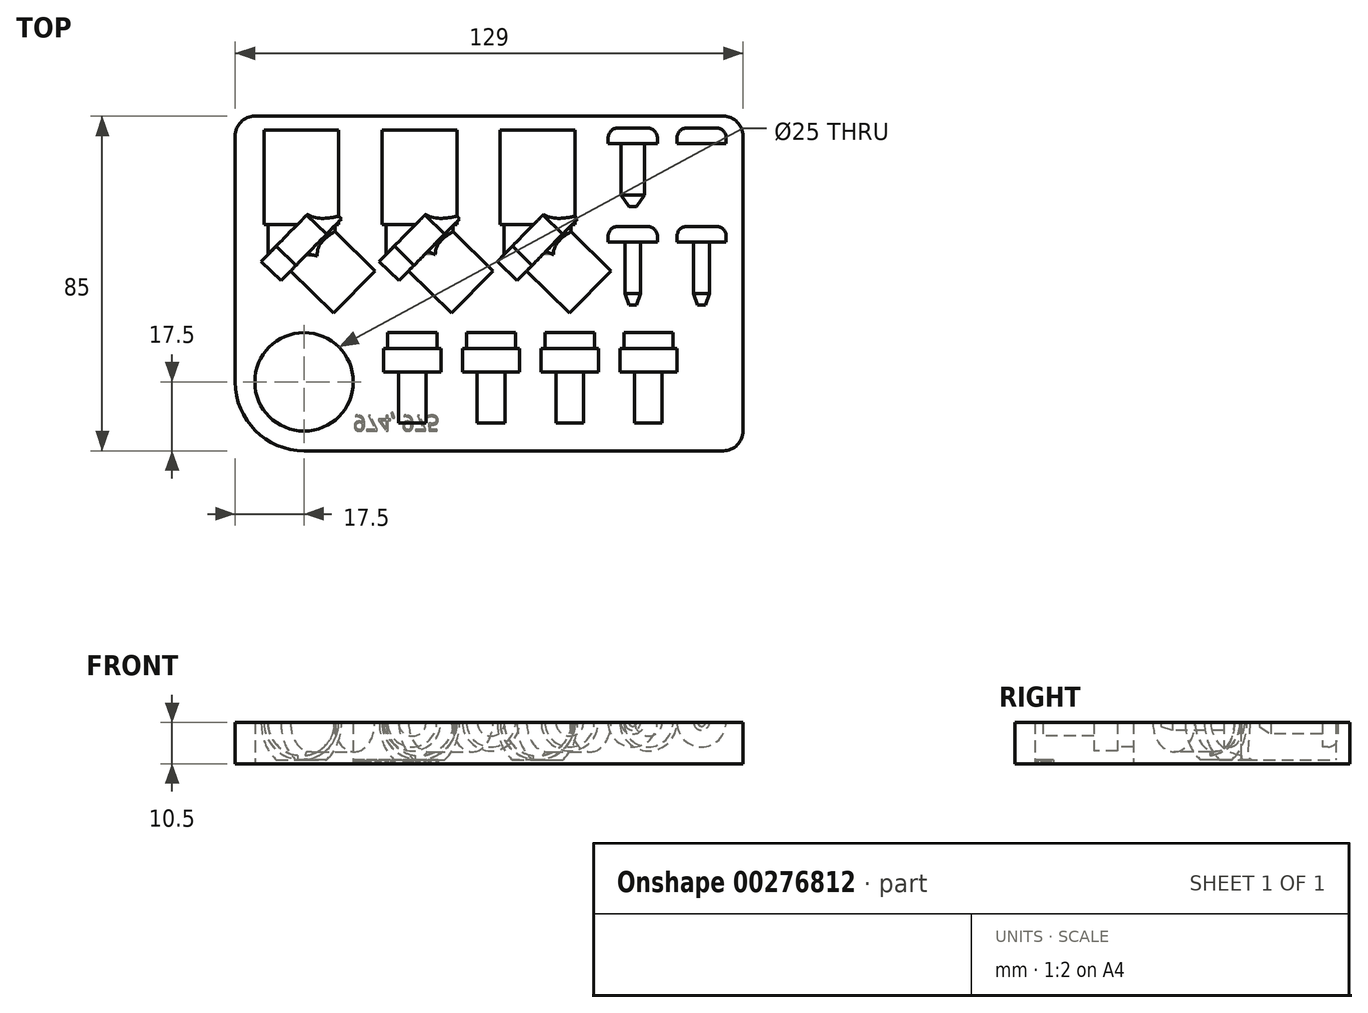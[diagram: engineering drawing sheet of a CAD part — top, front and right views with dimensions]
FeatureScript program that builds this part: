
annotation { "Feature Type Name" : "Feature", "Feature Type Description" : "" }
export const myFeature = defineFeature(function(context is Context, id is Id, definition is map)
    precondition{}
    {
        {
            var Q0;
            Q0=qCreatedBy(makeId("Top.planeOp"),FACE);
            var sketch = newSketch(context, id + "F0", { "sketchPlane" : qUnion([Q0])});
            skLineSegment(sketch, "E0.bottom", {"start": v(17.5, 0) * mm, "end": v(124, 0) * mm});
            skLineSegment(sketch, "E0.top", {"start": v(5, 85) * mm, "end": v(124, 85) * mm});
            skLineSegment(sketch, "E0.left", {"start": v(0, 17.5) * mm, "end": v(0, 80) * mm});
            skLineSegment(sketch, "E0.right", {"start": v(129, 5) * mm, "end": v(129, 80) * mm});
            skLineSegment(sketch, "E1.bottom", {"start": v(17.5, 0) * mm, "end": v(17.5, 0) * mm});
            skLineSegment(sketch, "E1.top", {"start": v(0, 17.5) * mm, "end": v(17.5, 17.5) * mm, "construction": true});
            skLineSegment(sketch, "E1.left", {"start": v(0, 17.5) * mm, "end": v(0, 17.5) * mm});
            skLineSegment(sketch, "E1.right", {"start": v(17.5, 0) * mm, "end": v(17.5, 17.5) * mm, "construction": true});
            skCircle(sketch, "E2", {"center": v(17.5, 17.5) * mm, "radius": 12.5 * mm});
            skPoint(sketch, "E3.visualSharp", {"position": v(0, 0) * mm});
            skArc(sketch, "E3.filletArc", {"start": v(0, 17.5) * mm, "mid": v(5.13, 5.13) * mm, "end": v(17.5, 0) * mm});
            skPoint(sketch, "E4.visualSharp", {"position": v(0, 85) * mm});
            skArc(sketch, "E4.filletArc", {"start": v(5, 85) * mm, "mid": v(1.46, 83.54) * mm, "end": v(0, 80) * mm});
            skPoint(sketch, "E5.visualSharp", {"position": v(129, 85) * mm});
            skArc(sketch, "E5.filletArc", {"start": v(129, 80) * mm, "mid": v(127.54, 83.54) * mm, "end": v(124, 85) * mm});
            skPoint(sketch, "E6.visualSharp", {"position": v(129, 0) * mm});
            skArc(sketch, "E6.filletArc", {"start": v(124, 0) * mm, "mid": v(127.54, 1.46) * mm, "end": v(129, 5) * mm});
            skSolve(sketch);
        }
        {
            var Q0;
            Q0=makeQuery(id+"F0.imprint","IMPRINT",FACE,{"disambiguationData":[TD([[makeQuery(id+"F0.imprint","IMPRINT",EDGE,{"derivedFrom":sQuery(id+"F0.wireOp",EDGE,"E0.bottom")}),1.0]])]});
            extrude(context, id + "F1", {"entities" : qUnion([Q0]), "depth" : 10.5 * mm});
        }
        {
            var Q0;
            Q0=makeQuery(id+"F1.opExtrude","CAP_FACE",FACE,{"disambiguationData":[OSD([sQuery(id+"F0.wireOp",EDGE,"E0.bottom"),sQuery(id+"F0.wireOp",EDGE,"E0.top"),sQuery(id+"F0.wireOp",EDGE,"E0.left"),sQuery(id+"F0.wireOp",EDGE,"E0.right"),sQuery(id+"F0.wireOp",EDGE,"E2"),sQuery(id+"F0.wireOp",EDGE,"E3.filletArc"),sQuery(id+"F0.wireOp",EDGE,"E4.filletArc"),sQuery(id+"F0.wireOp",EDGE,"E5.filletArc"),sQuery(id+"F0.wireOp",EDGE,"E6.filletArc")])],"isStart":false});
            var sketch = newSketch(context, id + "F2", { "sketchPlane" : qUnion([Q0])});
            skLineSegment(sketch, "E7.bottom", {"start": v(0, 0) * mm, "end": v(25, 0) * mm, "construction": true});
            skLineSegment(sketch, "E7.top", {"start": v(0, 35) * mm, "end": v(25, 35) * mm, "construction": true});
            skLineSegment(sketch, "E7.left", {"start": v(0, 0) * mm, "end": v(0, 35) * mm, "construction": true});
            skLineSegment(sketch, "E7.right", {"start": v(25, 0) * mm, "end": v(25, 35) * mm, "construction": true});
            skLineSegment(sketch, "E8", {"start": v(25, 35) * mm, "end": v(14.07, 45.7) * mm});
            skLineSegment(sketch, "E9", {"start": v(14.07, 45.7) * mm, "end": v(11.62, 43.2) * mm});
            skLineSegment(sketch, "E10", {"start": v(11.62, 43.2) * mm, "end": v(6.62, 48.1) * mm});
            skLineSegment(sketch, "E11", {"start": v(6.62, 48.1) * mm, "end": v(14.32, 55.96) * mm});
            skLineSegment(sketch, "E12", {"start": v(14.32, 55.96) * mm, "end": v(30.25, 40.36) * mm});
            skLineSegment(sketch, "E13", {"start": v(25, 35) * mm, "end": v(30.25, 40.36) * mm});
            skLineSegment(sketch, "E14", {"start": v(14.32, 55.96) * mm, "end": v(16.82, 53.51) * mm, "construction": true});
            skLineSegment(sketch, "E15", {"start": v(16.82, 53.51) * mm, "end": v(16.82, 81.51) * mm});
            skLineSegment(sketch, "E16", {"start": v(16.82, 81.51) * mm, "end": v(7.32, 81.51) * mm});
            skLineSegment(sketch, "E17", {"start": v(7.32, 81.51) * mm, "end": v(7.32, 57.51) * mm});
            skLineSegment(sketch, "E18", {"start": v(7.32, 57.51) * mm, "end": v(8.32, 57.51) * mm});
            skLineSegment(sketch, "E19", {"start": v(8.32, 57.51) * mm, "end": v(8.32, 53.16) * mm});
            skLineSegment(sketch, "E20", {"start": v(46.82, 53.51) * mm, "end": v(46.82, 81.51) * mm});
            skLineSegment(sketch, "E21", {"start": v(46.82, 81.51) * mm, "end": v(37.32, 81.51) * mm});
            skLineSegment(sketch, "E22", {"start": v(37.32, 81.51) * mm, "end": v(37.32, 57.51) * mm});
            skLineSegment(sketch, "E23", {"start": v(37.32, 57.51) * mm, "end": v(38.32, 57.51) * mm});
            skLineSegment(sketch, "E24", {"start": v(76.82, 53.51) * mm, "end": v(76.82, 81.51) * mm});
            skLineSegment(sketch, "E25", {"start": v(76.82, 81.51) * mm, "end": v(67.32, 81.51) * mm});
            skLineSegment(sketch, "E26", {"start": v(67.32, 81.51) * mm, "end": v(67.32, 57.51) * mm});
            skLineSegment(sketch, "E27", {"start": v(67.32, 57.51) * mm, "end": v(68.32, 57.51) * mm});
            skLineSegment(sketch, "E28", {"start": v(8.32, 57.51) * mm, "end": v(8.32, 49.51) * mm});
            skLineSegment(sketch, "E29", {"start": v(8.32, 49.51) * mm, "end": v(16.82, 53.51) * mm});
            skLineSegment(sketch, "E30", {"start": v(38.32, 57.51) * mm, "end": v(38.32, 49.51) * mm});
            skLineSegment(sketch, "E31", {"start": v(38.32, 49.51) * mm, "end": v(46.82, 53.51) * mm});
            skLineSegment(sketch, "E32", {"start": v(68.32, 57.51) * mm, "end": v(68.32, 49.51) * mm});
            skLineSegment(sketch, "E33", {"start": v(68.32, 49.51) * mm, "end": v(76.82, 53.51) * mm});
            skLineSegment(sketch, "E34", {"start": v(46.82, 53.51) * mm, "end": v(44.32, 55.96) * mm});
            skLineSegment(sketch, "E35", {"start": v(44.32, 55.96) * mm, "end": v(36.62, 48.1) * mm});
            skLineSegment(sketch, "E36", {"start": v(36.62, 48.1) * mm, "end": v(41.62, 43.2) * mm});
            skLineSegment(sketch, "E37", {"start": v(41.62, 43.2) * mm, "end": v(44.07, 45.7) * mm});
            skLineSegment(sketch, "E38", {"start": v(44.07, 45.7) * mm, "end": v(55, 35) * mm});
            skLineSegment(sketch, "E39", {"start": v(55, 35) * mm, "end": v(60.25, 40.36) * mm});
            skLineSegment(sketch, "E40", {"start": v(46.82, 53.51) * mm, "end": v(60.25, 40.36) * mm});
            skLineSegment(sketch, "E41", {"start": v(76.82, 53.51) * mm, "end": v(74.32, 55.96) * mm});
            skLineSegment(sketch, "E42", {"start": v(74.32, 55.96) * mm, "end": v(66.62, 48.1) * mm});
            skLineSegment(sketch, "E43", {"start": v(66.62, 48.1) * mm, "end": v(71.62, 43.2) * mm});
            skLineSegment(sketch, "E44", {"start": v(71.62, 43.2) * mm, "end": v(74.07, 45.7) * mm});
            skLineSegment(sketch, "E45", {"start": v(74.07, 45.7) * mm, "end": v(85, 35) * mm});
            skLineSegment(sketch, "E46", {"start": v(76.82, 53.51) * mm, "end": v(90.25, 40.36) * mm});
            skLineSegment(sketch, "E47", {"start": v(85, 35) * mm, "end": v(90.25, 40.36) * mm});
            skLineSegment(sketch, "E48", {"start": v(16.82, 53.51) * mm, "end": v(46.82, 53.51) * mm, "construction": true});
            skLineSegment(sketch, "E49", {"start": v(46.82, 53.51) * mm, "end": v(76.82, 53.51) * mm, "construction": true});
            skSolve(sketch);
        }
        {
            var Q0;
            {var subQ0=sQuery(id+"F2.wireOp",EDGE,"E15");Q0=makeQuery(id+"F2.imprint","IMPRINT",FACE,{"disambiguationData":[TD([[makeQuery(id+"F2.imprint","IMPRINT",EDGE,{"derivedFrom":subQ0}),1.0]])]});}
            var Q1;
            {var subQ5=sQuery(id+"F2.wireOp",EDGE,"E29");Q1=makeQuery(id+"F2.imprint","IMPRINT",FACE,{"disambiguationData":[TD([[makeQuery(id+"F2.imprint","IMPRINT",EDGE,{"derivedFrom":subQ5}),1.0]])]});}
            var Q2;
            Q2=sQuery(id+"F2.wireOp",EDGE,"E15");
            revolve(context, id + "F3", {"operationType" : NewBodyOperationType.REMOVE, "entities" : qUnion([Q0, Q1]), "axis" : qUnion([Q2]), "revolveType" : RevolveType.FULL, "oppositeDirection" : true});
        }
        {
            var Q0;
            Q0=makeQuery(id+"F2.imprint","IMPRINT",FACE,{"disambiguationData":[TD([[makeQuery(id+"F2.imprint","IMPRINT",EDGE,{"derivedFrom":sQuery(id+"F2.wireOp",EDGE,"E20")}),1.0]])]});
            var Q1;
            Q1=sQuery(id+"F2.wireOp",EDGE,"E20");
            revolve(context, id + "F4", {"operationType" : NewBodyOperationType.REMOVE, "entities" : qUnion([Q0]), "axis" : qUnion([Q1]), "revolveType" : RevolveType.FULL, "oppositeDirection" : true});
        }
        {
            var Q0;
            Q0=makeQuery(id+"F2.imprint","IMPRINT",FACE,{"disambiguationData":[TD([[makeQuery(id+"F2.imprint","IMPRINT",EDGE,{"derivedFrom":sQuery(id+"F2.wireOp",EDGE,"E24")}),1.0]])]});
            var Q1;
            Q1=sQuery(id+"F2.wireOp",EDGE,"E24");
            revolve(context, id + "F5", {"operationType" : NewBodyOperationType.REMOVE, "entities" : qUnion([Q0]), "axis" : qUnion([Q1]), "revolveType" : RevolveType.FULL, "oppositeDirection" : true});
        }
        {
            var Q0;
            Q0=makeQuery(id+"F2.imprint","IMPRINT",FACE,{"disambiguationData":[TD([[makeQuery(id+"F2.imprint","IMPRINT",EDGE,{"derivedFrom":sQuery(id+"F2.wireOp",EDGE,"E8")}),-1.0]])]});
            var Q1;
            {var subQ5=sQuery(id+"F2.wireOp",EDGE,"E29");Q1=makeQuery(id+"F2.imprint","IMPRINT",FACE,{"disambiguationData":[TD([[makeQuery(id+"F2.imprint","IMPRINT",EDGE,{"derivedFrom":subQ5}),1.0]])]});}
            var Q2;
            Q2=sQuery(id+"F2.wireOp",EDGE,"E12");
            revolve(context, id + "F6", {"operationType" : NewBodyOperationType.REMOVE, "entities" : qUnion([Q0, Q1]), "axis" : qUnion([Q2]), "revolveType" : RevolveType.FULL, "oppositeDirection" : true});
        }
        {
            var Q0;
            {var subQ4=sQuery(id+"F2.wireOp",EDGE,"E31");Q0=makeQuery(id+"F2.imprint","IMPRINT",FACE,{"disambiguationData":[TD([[makeQuery(id+"F2.imprint","IMPRINT",EDGE,{"derivedFrom":subQ4}),-1.0]])]});}
            var Q1;
            {var subQ0=sQuery(id+"F2.wireOp",EDGE,"E31");Q1=makeQuery(id+"F2.imprint","IMPRINT",FACE,{"disambiguationData":[TD([[makeQuery(id+"F2.imprint","IMPRINT",EDGE,{"derivedFrom":subQ0}),1.0]])]});}
            var Q2;
            Q2=sQuery(id+"F2.wireOp",EDGE,"E40");
            revolve(context, id + "F7", {"operationType" : NewBodyOperationType.REMOVE, "entities" : qUnion([Q0, Q1]), "axis" : qUnion([Q2]), "revolveType" : RevolveType.FULL, "oppositeDirection" : true});
        }
        {
            var Q0;
            {var subQ4=sQuery(id+"F2.wireOp",EDGE,"E33");Q0=makeQuery(id+"F2.imprint","IMPRINT",FACE,{"disambiguationData":[TD([[makeQuery(id+"F2.imprint","IMPRINT",EDGE,{"derivedFrom":subQ4}),-1.0]])]});}
            var Q1;
            {var subQ0=sQuery(id+"F2.wireOp",EDGE,"E33");Q1=makeQuery(id+"F2.imprint","IMPRINT",FACE,{"disambiguationData":[TD([[makeQuery(id+"F2.imprint","IMPRINT",EDGE,{"derivedFrom":subQ0}),1.0]])]});}
            var Q2;
            Q2=sQuery(id+"F2.wireOp",EDGE,"E46");
            revolve(context, id + "F8", {"operationType" : NewBodyOperationType.REMOVE, "entities" : qUnion([Q0, Q1]), "axis" : qUnion([Q2]), "revolveType" : RevolveType.FULL, "oppositeDirection" : true});
        }
        {
            var Q0;
            Q0=makeQuery(id+"F1.opExtrude","CAP_FACE",FACE,{"disambiguationData":[OSD([sQuery(id+"F0.wireOp",EDGE,"E0.bottom"),sQuery(id+"F0.wireOp",EDGE,"E0.top"),sQuery(id+"F0.wireOp",EDGE,"E0.left"),sQuery(id+"F0.wireOp",EDGE,"E0.right"),sQuery(id+"F0.wireOp",EDGE,"E2"),sQuery(id+"F0.wireOp",EDGE,"E3.filletArc"),sQuery(id+"F0.wireOp",EDGE,"E4.filletArc"),sQuery(id+"F0.wireOp",EDGE,"E5.filletArc"),sQuery(id+"F0.wireOp",EDGE,"E6.filletArc")])],"isStart":false});
            var sketch = newSketch(context, id + "F9", { "sketchPlane" : qUnion([Q0])});
            skLineSegment(sketch, "E50.0.0", {"start": v(124, 85) * mm, "end": v(5, 85) * mm});
            skArc(sketch, "E50.0.1", {"start": v(5, 85) * mm, "mid": v(1.46, 83.54) * mm, "end": v(0, 80) * mm});
            skLineSegment(sketch, "E50.0.2", {"start": v(0, 80) * mm, "end": v(0, 17.5) * mm});
            skArc(sketch, "E50.0.3", {"start": v(0, 17.5) * mm, "mid": v(5.13, 5.13) * mm, "end": v(17.5, 0) * mm});
            skLineSegment(sketch, "E50.0.4", {"start": v(17.5, 0) * mm, "end": v(124, 0) * mm});
            skArc(sketch, "E50.0.5", {"start": v(124, 0) * mm, "mid": v(127.54, 1.46) * mm, "end": v(129, 5) * mm});
            skLineSegment(sketch, "E50.0.6", {"start": v(129, 5) * mm, "end": v(129, 80) * mm});
            skArc(sketch, "E50.0.7", {"start": v(129, 80) * mm, "mid": v(127.54, 83.54) * mm, "end": v(124, 85) * mm});
            skCircle(sketch, "E51.0", {"center": v(17.5, 17.5) * mm, "radius": 12.5 * mm});
            skSolve(sketch);
        }
        {
            var Q0;
            Q0=qSketchRegion(id+"F9",true);
            extrude(context, id + "F10", {"entities" : qUnion([Q0]), "operationType" : NewBodyOperationType.ADD, "oppositeDirection" : true, "depth" : 10.5 * mm, "hasSecondDirection" : true, "secondDirectionOppositeDirection" : true, "secondDirectionDepth" : 9.5 * mm});
        }
        {
            var Q0;
            Q0=makeQuery(id+"F1.opExtrude","CAP_FACE",FACE,{"disambiguationData":[OSD([sQuery(id+"F0.wireOp",EDGE,"E0.bottom"),sQuery(id+"F0.wireOp",EDGE,"E0.top"),sQuery(id+"F0.wireOp",EDGE,"E0.left"),sQuery(id+"F0.wireOp",EDGE,"E0.right"),sQuery(id+"F0.wireOp",EDGE,"E2"),sQuery(id+"F0.wireOp",EDGE,"E3.filletArc"),sQuery(id+"F0.wireOp",EDGE,"E4.filletArc"),sQuery(id+"F0.wireOp",EDGE,"E5.filletArc"),sQuery(id+"F0.wireOp",EDGE,"E6.filletArc")])],"isStart":false});
            var sketch = newSketch(context, id + "F11", { "sketchPlane" : qUnion([Q0])});
            skLineSegment(sketch, "E52.bottom", {"start": v(0, 0) * mm, "end": v(101, 0) * mm, "construction": true});
            skLineSegment(sketch, "E52.top", {"start": v(0, 82) * mm, "end": v(101, 82) * mm, "construction": true});
            skLineSegment(sketch, "E52.left", {"start": v(0, 0) * mm, "end": v(0, 82) * mm, "construction": true});
            skLineSegment(sketch, "E52.right", {"start": v(101, 0) * mm, "end": v(101, 82) * mm, "construction": true});
            skLineSegment(sketch, "E53.bottom", {"start": v(101, 82) * mm, "end": v(104.75, 82) * mm});
            skLineSegment(sketch, "E53.top", {"start": v(104, 78) * mm, "end": v(107.25, 78) * mm});
            skLineSegment(sketch, "E53.left", {"start": v(101, 82) * mm, "end": v(101, 78) * mm});
            skLineSegment(sketch, "E53.right", {"start": v(107.25, 79.5) * mm, "end": v(107.25, 78) * mm});
            skPoint(sketch, "E54.visualSharp", {"position": v(107.25, 82) * mm});
            skArc(sketch, "E54.filletArc", {"start": v(107.25, 79.5) * mm, "mid": v(106.52, 81.27) * mm, "end": v(104.75, 82) * mm});
            skLineSegment(sketch, "E55.left", {"start": v(101, 78) * mm, "end": v(101, 72) * mm});
            skLineSegment(sketch, "E55.right", {"start": v(104, 78) * mm, "end": v(104, 65) * mm});
            skLineSegment(sketch, "E56", {"start": v(101, 82) * mm, "end": v(118.5, 82) * mm, "construction": true});
            skLineSegment(sketch, "E57.bottom", {"start": v(118.5, 82) * mm, "end": v(122.25, 82) * mm});
            skLineSegment(sketch, "E57.top", {"start": v(118.5, 78) * mm, "end": v(124.75, 78) * mm});
            skLineSegment(sketch, "E57.left", {"start": v(118.5, 82) * mm, "end": v(118.5, 78) * mm});
            skLineSegment(sketch, "E57.right", {"start": v(124.75, 79.5) * mm, "end": v(124.75, 78) * mm});
            skLineSegment(sketch, "E58.bottom", {"start": v(118.5, 78) * mm, "end": v(121.5, 78) * mm});
            skLineSegment(sketch, "E58.top", {"start": v(118.5, 62) * mm, "end": v(119.5, 62) * mm});
            skLineSegment(sketch, "E58.left", {"start": v(118.5, 78) * mm, "end": v(118.5, 62) * mm});
            skLineSegment(sketch, "E58.right", {"start": v(121.5, 78) * mm, "end": v(121.5, 65) * mm});
            skPoint(sketch, "E59.visualSharp", {"position": v(124.75, 82) * mm});
            skArc(sketch, "E59.filletArc", {"start": v(124.75, 79.5) * mm, "mid": v(124.02, 81.27) * mm, "end": v(122.25, 82) * mm});
            skLineSegment(sketch, "E60", {"start": v(118.5, 62) * mm, "end": v(119.5, 62) * mm, "construction": true});
            skLineSegment(sketch, "E61", {"start": v(119.5, 62) * mm, "end": v(121.5, 65) * mm});
            skLineSegment(sketch, "E62", {"start": v(101, 78) * mm, "end": v(101, 62) * mm});
            skLineSegment(sketch, "E63", {"start": v(101, 62) * mm, "end": v(102, 62) * mm});
            skLineSegment(sketch, "E64", {"start": v(102, 62) * mm, "end": v(104, 65) * mm});
            skLineSegment(sketch, "E65", {"start": v(101, 62) * mm, "end": v(101, 57) * mm, "construction": true});
            skLineSegment(sketch, "E66.bottom", {"start": v(101, 57) * mm, "end": v(104.75, 57) * mm});
            skLineSegment(sketch, "E66.top", {"start": v(103, 53) * mm, "end": v(107.25, 53) * mm});
            skLineSegment(sketch, "E66.left", {"start": v(101, 57) * mm, "end": v(101, 53) * mm});
            skLineSegment(sketch, "E66.right", {"start": v(107.25, 54.5) * mm, "end": v(107.25, 53) * mm});
            skLineSegment(sketch, "E67.left", {"start": v(101, 53) * mm, "end": v(101, 37) * mm});
            skLineSegment(sketch, "E68", {"start": v(103, 53) * mm, "end": v(103, 40) * mm});
            skLineSegment(sketch, "E69", {"start": v(101, 37) * mm, "end": v(102, 37) * mm});
            skLineSegment(sketch, "E70", {"start": v(102, 37) * mm, "end": v(103, 40) * mm});
            skPoint(sketch, "E71.visualSharp", {"position": v(107.25, 57) * mm});
            skArc(sketch, "E71.filletArc", {"start": v(107.25, 54.5) * mm, "mid": v(106.52, 56.27) * mm, "end": v(104.75, 57) * mm});
            skLineSegment(sketch, "E72", {"start": v(101, 57) * mm, "end": v(118.5, 57) * mm, "construction": true});
            skLineSegment(sketch, "E73.bottom", {"start": v(118.5, 57) * mm, "end": v(122.25, 57) * mm});
            skLineSegment(sketch, "E73.top", {"start": v(120.5, 53) * mm, "end": v(124.75, 53) * mm});
            skLineSegment(sketch, "E73.left", {"start": v(118.5, 57) * mm, "end": v(118.5, 53) * mm});
            skLineSegment(sketch, "E73.right", {"start": v(124.75, 54.5) * mm, "end": v(124.75, 53) * mm});
            skLineSegment(sketch, "E74.left", {"start": v(118.5, 53) * mm, "end": v(118.5, 37) * mm});
            skLineSegment(sketch, "E75", {"start": v(120.5, 53) * mm, "end": v(120.5, 40) * mm});
            skLineSegment(sketch, "E76", {"start": v(118.5, 37) * mm, "end": v(119.5, 37) * mm});
            skLineSegment(sketch, "E77", {"start": v(119.5, 37) * mm, "end": v(120.5, 40) * mm});
            skPoint(sketch, "E78.visualSharp", {"position": v(124.75, 57) * mm});
            skArc(sketch, "E78.filletArc", {"start": v(124.75, 54.5) * mm, "mid": v(124.02, 56.27) * mm, "end": v(122.25, 57) * mm});
            skSolve(sketch);
        }
        {
            var Q0;
            Q0=makeQuery(id+"F11.imprint","IMPRINT",FACE,{"disambiguationData":[TD([[makeQuery(id+"F11.imprint","IMPRINT",EDGE,{"derivedFrom":sQuery(id+"F11.wireOp",EDGE,"E53.bottom")}),-1.0]])]});
            var Q1;
            Q1=makeQuery(id+"F11.imprint","IMPRINT",FACE,{"disambiguationData":[TD([[makeQuery(id+"F11.imprint","IMPRINT",EDGE,{"derivedFrom":sQuery(id+"F11.wireOp",EDGE,"E66.bottom")}),-1.0]])]});
            var Q2;
            Q2=sQuery(id+"F11.wireOp",EDGE,"E67.left");
            revolve(context, id + "F12", {"operationType" : NewBodyOperationType.REMOVE, "entities" : qUnion([Q0, Q1]), "axis" : qUnion([Q2]), "revolveType" : RevolveType.FULL, "oppositeDirection" : true});
        }
        {
            var Q0;
            Q0=makeQuery(id+"F11.imprint","IMPRINT",FACE,{"disambiguationData":[TD([[makeQuery(id+"F11.imprint","IMPRINT",EDGE,{"derivedFrom":sQuery(id+"F11.wireOp",EDGE,"E58.bottom")}),-1.0]])]});
            var Q1;
            Q1=makeQuery(id+"F11.imprint","IMPRINT",FACE,{"disambiguationData":[TD([[makeQuery(id+"F11.imprint","IMPRINT",EDGE,{"derivedFrom":sQuery(id+"F11.wireOp",EDGE,"E57.bottom")}),-1.0]])]});
            var Q2;
            Q2=makeQuery(id+"F11.imprint","IMPRINT",FACE,{"disambiguationData":[TD([[makeQuery(id+"F11.imprint","IMPRINT",EDGE,{"derivedFrom":sQuery(id+"F11.wireOp",EDGE,"E73.bottom")}),-1.0]])]});
            var Q3;
            Q3=sQuery(id+"F11.wireOp",EDGE,"E74.left");
            revolve(context, id + "F13", {"operationType" : NewBodyOperationType.REMOVE, "entities" : qUnion([Q0, Q1, Q2]), "axis" : qUnion([Q3]), "revolveType" : RevolveType.FULL, "oppositeDirection" : true});
        }
        {
            var Q0;
            Q0=makeQuery(id+"F1.opExtrude","CAP_FACE",FACE,{"disambiguationData":[OSD([sQuery(id+"F0.wireOp",EDGE,"E0.bottom"),sQuery(id+"F0.wireOp",EDGE,"E0.top"),sQuery(id+"F0.wireOp",EDGE,"E0.left"),sQuery(id+"F0.wireOp",EDGE,"E0.right"),sQuery(id+"F0.wireOp",EDGE,"E2"),sQuery(id+"F0.wireOp",EDGE,"E3.filletArc"),sQuery(id+"F0.wireOp",EDGE,"E4.filletArc"),sQuery(id+"F0.wireOp",EDGE,"E5.filletArc"),sQuery(id+"F0.wireOp",EDGE,"E6.filletArc")])],"isStart":false});
            var sketch = newSketch(context, id + "F14", { "sketchPlane" : qUnion([Q0])});
            skLineSegment(sketch, "E79.bottom", {"start": v(0, 0) * mm, "end": v(45, 0) * mm, "construction": true});
            skLineSegment(sketch, "E79.top", {"start": v(0, 30) * mm, "end": v(45, 30) * mm, "construction": true});
            skLineSegment(sketch, "E79.left", {"start": v(0, 0) * mm, "end": v(0, 30) * mm, "construction": true});
            skLineSegment(sketch, "E79.right", {"start": v(45, 0) * mm, "end": v(45, 17.5) * mm, "construction": true});
            skLineSegment(sketch, "E80.bottom", {"start": v(45, 30) * mm, "end": v(51.25, 30) * mm});
            skLineSegment(sketch, "E80.left", {"start": v(45, 30) * mm, "end": v(45, 26) * mm});
            skLineSegment(sketch, "E80.right", {"start": v(51.25, 30) * mm, "end": v(51.25, 26) * mm});
            skLineSegment(sketch, "E81.bottom", {"start": v(51.25, 26) * mm, "end": v(52.25, 26) * mm});
            skLineSegment(sketch, "E81.left", {"start": v(45, 26) * mm, "end": v(45, 17.5) * mm});
            skPoint(sketch, "E81.right.end.orphan", {"position": v(47.25, 17.5) * mm});
            skLineSegment(sketch, "E82.trimOffspring", {"start": v(45, 26) * mm, "end": v(45, 30) * mm, "construction": true});
            skLineSegment(sketch, "E83", {"start": v(52.25, 26) * mm, "end": v(52.25, 20) * mm});
            skLineSegment(sketch, "E84", {"start": v(52.25, 20) * mm, "end": v(48.5, 20) * mm});
            skLineSegment(sketch, "E85", {"start": v(45, 20) * mm, "end": v(45, 26) * mm});
            skLineSegment(sketch, "E86.top", {"start": v(45, 7) * mm, "end": v(48.5, 7) * mm});
            skLineSegment(sketch, "E86.left", {"start": v(45, 20) * mm, "end": v(45, 7) * mm});
            skLineSegment(sketch, "E86.right", {"start": v(48.5, 20) * mm, "end": v(48.5, 7) * mm});
            skLineSegment(sketch, "E87", {"start": v(45, 30) * mm, "end": v(65, 30) * mm, "construction": true});
            skLineSegment(sketch, "E88", {"start": v(65, 30) * mm, "end": v(85, 30) * mm, "construction": true});
            skLineSegment(sketch, "E89", {"start": v(85, 30) * mm, "end": v(105, 30) * mm, "construction": true});
            skLineSegment(sketch, "E90.bottom", {"start": v(65, 30) * mm, "end": v(71.25, 30) * mm});
            skLineSegment(sketch, "E90.left", {"start": v(65, 30) * mm, "end": v(65, 26) * mm});
            skLineSegment(sketch, "E90.right", {"start": v(71.25, 30) * mm, "end": v(71.25, 26) * mm});
            skLineSegment(sketch, "E91.bottom", {"start": v(85, 30) * mm, "end": v(91.25, 30) * mm});
            skLineSegment(sketch, "E91.left", {"start": v(85, 30) * mm, "end": v(85, 26) * mm});
            skLineSegment(sketch, "E91.right", {"start": v(91.25, 30) * mm, "end": v(91.25, 26) * mm});
            skLineSegment(sketch, "E92.bottom", {"start": v(105, 30) * mm, "end": v(111.25, 30) * mm});
            skLineSegment(sketch, "E92.left", {"start": v(105, 30) * mm, "end": v(105, 26) * mm});
            skLineSegment(sketch, "E92.right", {"start": v(111.25, 30) * mm, "end": v(111.25, 26) * mm});
            skLineSegment(sketch, "E93.bottom", {"start": v(71.25, 26) * mm, "end": v(72.25, 26) * mm});
            skLineSegment(sketch, "E93.top", {"start": v(68.5, 20) * mm, "end": v(72.25, 20) * mm});
            skLineSegment(sketch, "E93.left", {"start": v(65, 26) * mm, "end": v(65, 20) * mm});
            skLineSegment(sketch, "E93.right", {"start": v(72.25, 26) * mm, "end": v(72.25, 20) * mm});
            skLineSegment(sketch, "E94.bottom", {"start": v(91.25, 26) * mm, "end": v(92.25, 26) * mm});
            skLineSegment(sketch, "E94.top", {"start": v(88.5, 20) * mm, "end": v(92.25, 20) * mm});
            skLineSegment(sketch, "E94.left", {"start": v(85, 26) * mm, "end": v(85, 20) * mm});
            skLineSegment(sketch, "E94.right", {"start": v(92.25, 26) * mm, "end": v(92.25, 20) * mm});
            skLineSegment(sketch, "E95.bottom", {"start": v(111.25, 26) * mm, "end": v(112.25, 26) * mm});
            skLineSegment(sketch, "E95.top", {"start": v(108.5, 20) * mm, "end": v(112.25, 20) * mm});
            skLineSegment(sketch, "E95.left", {"start": v(105, 26) * mm, "end": v(105, 20) * mm});
            skLineSegment(sketch, "E95.right", {"start": v(112.25, 26) * mm, "end": v(112.25, 20) * mm});
            skLineSegment(sketch, "E96.top", {"start": v(65, 7) * mm, "end": v(68.5, 7) * mm});
            skLineSegment(sketch, "E96.left", {"start": v(65, 20) * mm, "end": v(65, 7) * mm});
            skLineSegment(sketch, "E96.right", {"start": v(68.5, 20) * mm, "end": v(68.5, 7) * mm});
            skLineSegment(sketch, "E97.top", {"start": v(85, 7) * mm, "end": v(88.5, 7) * mm});
            skLineSegment(sketch, "E97.left", {"start": v(85, 20) * mm, "end": v(85, 7) * mm});
            skLineSegment(sketch, "E97.right", {"start": v(88.5, 20) * mm, "end": v(88.5, 7) * mm});
            skLineSegment(sketch, "E98.top", {"start": v(105, 7) * mm, "end": v(108.5, 7) * mm});
            skLineSegment(sketch, "E98.left", {"start": v(105, 20) * mm, "end": v(105, 7) * mm});
            skLineSegment(sketch, "E98.right", {"start": v(108.5, 20) * mm, "end": v(108.5, 7) * mm});
            skSolve(sketch);
        }
        {
            var Q0;
            Q0=makeQuery(id+"F14.imprint","IMPRINT",FACE,{"disambiguationData":[TD([[makeQuery(id+"F14.imprint","IMPRINT",EDGE,{"derivedFrom":sQuery(id+"F14.wireOp",EDGE,"E80.bottom")}),-1.0]])]});
            var Q1;
            Q1=sQuery(id+"F14.wireOp",EDGE,"E86.left");
            revolve(context, id + "F15", {"operationType" : NewBodyOperationType.REMOVE, "entities" : qUnion([Q0]), "axis" : qUnion([Q1]), "revolveType" : RevolveType.FULL, "oppositeDirection" : true});
        }
        {
            var Q0;
            Q0=makeQuery(id+"F14.imprint","IMPRINT",FACE,{"disambiguationData":[TD([[makeQuery(id+"F14.imprint","IMPRINT",EDGE,{"derivedFrom":sQuery(id+"F14.wireOp",EDGE,"E90.bottom")}),-1.0]])]});
            var Q1;
            Q1=sQuery(id+"F14.wireOp",EDGE,"E96.left");
            revolve(context, id + "F16", {"operationType" : NewBodyOperationType.REMOVE, "entities" : qUnion([Q0]), "axis" : qUnion([Q1]), "revolveType" : RevolveType.FULL, "oppositeDirection" : true});
        }
        {
            var Q0;
            Q0=makeQuery(id+"F14.imprint","IMPRINT",FACE,{"disambiguationData":[TD([[makeQuery(id+"F14.imprint","IMPRINT",EDGE,{"derivedFrom":sQuery(id+"F14.wireOp",EDGE,"E91.bottom")}),-1.0]])]});
            var Q1;
            Q1=sQuery(id+"F14.wireOp",EDGE,"E97.left");
            revolve(context, id + "F17", {"operationType" : NewBodyOperationType.REMOVE, "entities" : qUnion([Q0]), "axis" : qUnion([Q1]), "revolveType" : RevolveType.FULL, "oppositeDirection" : true});
        }
        {
            var Q0;
            Q0=makeQuery(id+"F14.imprint","IMPRINT",FACE,{"disambiguationData":[TD([[makeQuery(id+"F14.imprint","IMPRINT",EDGE,{"derivedFrom":sQuery(id+"F14.wireOp",EDGE,"E92.bottom")}),-1.0]])]});
            var Q1;
            Q1=sQuery(id+"F14.wireOp",EDGE,"E98.left");
            revolve(context, id + "F18", {"operationType" : NewBodyOperationType.REMOVE, "entities" : qUnion([Q0]), "axis" : qUnion([Q1]), "revolveType" : RevolveType.FULL, "oppositeDirection" : true});
        }
        {
            var Q0;
            Q0=makeQuery(id+"F10.boolean.opBoolean","MERGE",FACE,{"derivedFrom":[makeQuery(id+"F1.opExtrude","CAP_FACE",FACE,{"disambiguationData":[OSD([sQuery(id+"F0.wireOp",EDGE,"E0.bottom"),sQuery(id+"F0.wireOp",EDGE,"E0.top"),sQuery(id+"F0.wireOp",EDGE,"E0.left"),sQuery(id+"F0.wireOp",EDGE,"E0.right"),sQuery(id+"F0.wireOp",EDGE,"E2"),sQuery(id+"F0.wireOp",EDGE,"E3.filletArc"),sQuery(id+"F0.wireOp",EDGE,"E4.filletArc"),sQuery(id+"F0.wireOp",EDGE,"E5.filletArc"),sQuery(id+"F0.wireOp",EDGE,"E6.filletArc")])],"isStart":true}),makeQuery(id+"F10.opExtrude","CAP_FACE",FACE,{"disambiguationData":[OSD([sQuery(id+"F9.wireOp",EDGE,"E50.0.0"),sQuery(id+"F9.wireOp",EDGE,"E50.0.1"),sQuery(id+"F9.wireOp",EDGE,"E50.0.2"),sQuery(id+"F9.wireOp",EDGE,"E50.0.3"),sQuery(id+"F9.wireOp",EDGE,"E50.0.4"),sQuery(id+"F9.wireOp",EDGE,"E50.0.5"),sQuery(id+"F9.wireOp",EDGE,"E50.0.6"),sQuery(id+"F9.wireOp",EDGE,"E50.0.7"),sQuery(id+"F9.wireOp",EDGE,"E51.0")])],"isStart":false})]});
            var sketch = newSketch(context, id + "F19", { "sketchPlane" : qUnion([Q0])});
            skLineSegment(sketch, "E99.bottom", {"start": v(0, 0) * mm, "end": v(30, 0) * mm, "construction": true});
            skLineSegment(sketch, "E99.top", {"start": v(0, -5) * mm, "end": v(30, -5) * mm, "construction": true});
            skLineSegment(sketch, "E99.left", {"start": v(0, 0) * mm, "end": v(0, -5) * mm, "construction": true});
            skLineSegment(sketch, "E99.right", {"start": v(30, 0) * mm, "end": v(30, -5) * mm, "construction": true});
            skText(sketch, "E100", { "text": "974, 975", "fontName": "OpenSans-Regular.ttf"});
            const initialGuessF19  = {"E100": [0.03, -0.009, 1, 0, 0.004]};
            skSetInitialGuess(sketch, initialGuessF19);
            skSolve(sketch);
        }
        {
            var Q0;
            Q0 = qSketchRegion(id + "F19", true);
            extrude(context, id + "F20", {"entities" : qUnion([Q0]), "operationType" : NewBodyOperationType.REMOVE, "oppositeDirection" : true, "depth" : 1 * mm});
        }
        {
            var Q0;
            Q0=makeQuery(id+"F1.opExtrude","CAP_FACE",FACE,{"disambiguationData":[OSD([sQuery(id+"F0.wireOp",EDGE,"E0.bottom"),sQuery(id+"F0.wireOp",EDGE,"E0.top"),sQuery(id+"F0.wireOp",EDGE,"E0.left"),sQuery(id+"F0.wireOp",EDGE,"E0.right"),sQuery(id+"F0.wireOp",EDGE,"E2"),sQuery(id+"F0.wireOp",EDGE,"E3.filletArc"),sQuery(id+"F0.wireOp",EDGE,"E4.filletArc"),sQuery(id+"F0.wireOp",EDGE,"E5.filletArc"),sQuery(id+"F0.wireOp",EDGE,"E6.filletArc")])],"isStart":false});
            var sketch = newSketch(context, id + "F21", { "sketchPlane" : qUnion([Q0])});
            skLineSegment(sketch, "E101.0", {"start": v(0, 17.5) * mm, "end": v(0, 80) * mm});
            skArc(sketch, "E102.0", {"start": v(5, 85) * mm, "mid": v(1.46, 83.54) * mm, "end": v(0, 80) * mm});
            skLineSegment(sketch, "E103.0", {"start": v(5, 85) * mm, "end": v(124, 85) * mm});
            skArc(sketch, "E104.0", {"start": v(129, 80) * mm, "mid": v(127.54, 83.54) * mm, "end": v(124, 85) * mm});
            skLineSegment(sketch, "E105.0", {"start": v(129, 5) * mm, "end": v(129, 80) * mm});
            skArc(sketch, "E106.0", {"start": v(124, 0) * mm, "mid": v(127.54, 1.46) * mm, "end": v(129, 5) * mm});
            skLineSegment(sketch, "E107.0", {"start": v(17.5, 0) * mm, "end": v(124, 0) * mm});
            skLineSegment(sketch, "E108.0", {"start": v(98.75, 30) * mm, "end": v(111.25, 30) * mm});
            skLineSegment(sketch, "E109.0", {"start": v(98.75, 26) * mm, "end": v(98.75, 30) * mm});
            skLineSegment(sketch, "E110.0", {"start": v(97.75, 26) * mm, "end": v(98.75, 26) * mm});
            skLineSegment(sketch, "E111.0", {"start": v(97.75, 20) * mm, "end": v(97.75, 26) * mm});
            skLineSegment(sketch, "E112.0", {"start": v(97.75, 20) * mm, "end": v(101.5, 20) * mm});
            skLineSegment(sketch, "E113.0", {"start": v(101.5, 7) * mm, "end": v(101.5, 20) * mm});
            skLineSegment(sketch, "E114.0", {"start": v(108.5, 20) * mm, "end": v(108.5, 7) * mm});
            skLineSegment(sketch, "E115.0", {"start": v(112.25, 26) * mm, "end": v(112.25, 20) * mm});
            skPoint(sketch, "E116.0", {"position": v(111.75, 26) * mm});
            skLineSegment(sketch, "E117.0", {"start": v(111.25, 26) * mm, "end": v(112.25, 26) * mm});
            skLineSegment(sketch, "E118.0", {"start": v(111.25, 30) * mm, "end": v(111.25, 26) * mm});
            skLineSegment(sketch, "E119.0", {"start": v(108.5, 20) * mm, "end": v(112.25, 20) * mm});
            skLineSegment(sketch, "E120.0", {"start": v(101.5, 7) * mm, "end": v(108.5, 7) * mm});
            skLineSegment(sketch, "E121.0", {"start": v(81.5, 7) * mm, "end": v(88.5, 7) * mm});
            skLineSegment(sketch, "E122.0", {"start": v(81.5, 7) * mm, "end": v(81.5, 20) * mm});
            skLineSegment(sketch, "E123.0", {"start": v(88.5, 20) * mm, "end": v(88.5, 7) * mm});
            skLineSegment(sketch, "E124.0", {"start": v(88.5, 20) * mm, "end": v(92.25, 20) * mm});
            skLineSegment(sketch, "E125.0", {"start": v(92.25, 26) * mm, "end": v(92.25, 20) * mm});
            skLineSegment(sketch, "E126.0", {"start": v(91.25, 26) * mm, "end": v(92.25, 26) * mm});
            skLineSegment(sketch, "E127.0", {"start": v(91.25, 30) * mm, "end": v(91.25, 26) * mm});
            skPoint(sketch, "E128.0", {"position": v(78.25, 26) * mm});
            skLineSegment(sketch, "E129.0", {"start": v(77.75, 20) * mm, "end": v(77.75, 26) * mm});
            skLineSegment(sketch, "E130.0", {"start": v(77.75, 20) * mm, "end": v(81.5, 20) * mm});
            skLineSegment(sketch, "E131.0", {"start": v(77.75, 26) * mm, "end": v(78.75, 26) * mm});
            skLineSegment(sketch, "E132.0", {"start": v(78.75, 26) * mm, "end": v(78.75, 30) * mm});
            skLineSegment(sketch, "E133.0", {"start": v(78.75, 30) * mm, "end": v(91.25, 30) * mm});
            skLineSegment(sketch, "E134.0", {"start": v(58.75, 26) * mm, "end": v(58.75, 30) * mm});
            skLineSegment(sketch, "E135.0", {"start": v(58.75, 30) * mm, "end": v(71.25, 30) * mm});
            skLineSegment(sketch, "E136.0", {"start": v(71.25, 30) * mm, "end": v(71.25, 26) * mm});
            skLineSegment(sketch, "E137.0", {"start": v(71.25, 26) * mm, "end": v(72.25, 26) * mm});
            skLineSegment(sketch, "E138.0", {"start": v(72.25, 26) * mm, "end": v(72.25, 20) * mm});
            skLineSegment(sketch, "E139.0", {"start": v(68.5, 20) * mm, "end": v(72.25, 20) * mm});
            skLineSegment(sketch, "E140.0", {"start": v(68.5, 20) * mm, "end": v(68.5, 7) * mm});
            skLineSegment(sketch, "E141.0", {"start": v(61.5, 7) * mm, "end": v(68.5, 7) * mm});
            skLineSegment(sketch, "E142.0", {"start": v(61.5, 7) * mm, "end": v(61.5, 20) * mm});
            skLineSegment(sketch, "E143.0", {"start": v(57.75, 20) * mm, "end": v(61.5, 20) * mm});
            skLineSegment(sketch, "E144.0", {"start": v(57.75, 20) * mm, "end": v(57.75, 26) * mm});
            skLineSegment(sketch, "E145.0", {"start": v(52.25, 20) * mm, "end": v(48.5, 20) * mm});
            skLineSegment(sketch, "E146.0", {"start": v(48.5, 20) * mm, "end": v(48.5, 7) * mm});
            skLineSegment(sketch, "E147.0", {"start": v(52.25, 26) * mm, "end": v(52.25, 20) * mm});
            skLineSegment(sketch, "E148.0", {"start": v(41.5, 7) * mm, "end": v(48.5, 7) * mm});
            skLineSegment(sketch, "E149.0", {"start": v(41.5, 7) * mm, "end": v(41.5, 20) * mm});
            skLineSegment(sketch, "E150.0", {"start": v(41.5, 20) * mm, "end": v(37.75, 20) * mm});
            skLineSegment(sketch, "E151.0", {"start": v(37.75, 20) * mm, "end": v(37.75, 26) * mm});
            skLineSegment(sketch, "E152.0", {"start": v(37.75, 26) * mm, "end": v(38.75, 26) * mm});
            skLineSegment(sketch, "E153.0", {"start": v(38.75, 26) * mm, "end": v(38.75, 30) * mm});
            skLineSegment(sketch, "E154.0", {"start": v(38.75, 30) * mm, "end": v(51.25, 30) * mm});
            skPoint(sketch, "E155.0", {"position": v(51.25, 28) * mm});
            skLineSegment(sketch, "E156.0", {"start": v(51.25, 30) * mm, "end": v(51.25, 26) * mm});
            skLineSegment(sketch, "E157.0", {"start": v(51.25, 26) * mm, "end": v(52.25, 26) * mm});
            skCircle(sketch, "E158.0", {"center": v(17.5, 17.5) * mm, "radius": 12.5 * mm});
            skArc(sketch, "E159.0", {"start": v(0, 17.5) * mm, "mid": v(5.13, 5.13) * mm, "end": v(17.5, 0) * mm});
            skLineSegment(sketch, "E160.0", {"start": v(35.5, 45.72) * mm, "end": v(25.32, 55.69) * mm});
            skLineSegment(sketch, "E161.0", {"start": v(35.5, 45.72) * mm, "end": v(25, 35) * mm});
            skLineSegment(sketch, "E162.0", {"start": v(14.07, 45.7) * mm, "end": v(25, 35) * mm});
            skLineSegment(sketch, "E163.0", {"start": v(11.62, 43.2) * mm, "end": v(14.07, 45.7) * mm});
            skLineSegment(sketch, "E164.0", {"start": v(6.62, 48.1) * mm, "end": v(11.62, 43.2) * mm});
            skLineSegment(sketch, "E165.0", {"start": v(8.32, 49.84) * mm, "end": v(6.62, 48.1) * mm});
            skLineSegment(sketch, "E166.0", {"start": v(8.32, 57.51) * mm, "end": v(8.32, 49.84) * mm});
            skLineSegment(sketch, "E167.0", {"start": v(25.32, 55.69) * mm, "end": v(25.32, 57.19) * mm});
            skLineSegment(sketch, "E168.0", {"start": v(25.32, 57.19) * mm, "end": v(25.64, 57.51) * mm});
            skLineSegment(sketch, "E169.0", {"start": v(25.64, 57.51) * mm, "end": v(26.32, 57.51) * mm});
            skLineSegment(sketch, "E170.0", {"start": v(26.32, 57.51) * mm, "end": v(26.32, 58.2) * mm});
            skLineSegment(sketch, "E171.0", {"start": v(26.32, 58.2) * mm, "end": v(27.02, 58.92) * mm});
            skLineSegment(sketch, "E172.0", {"start": v(27.02, 58.92) * mm, "end": v(26.32, 59.6) * mm});
            skLineSegment(sketch, "E173.0", {"start": v(26.32, 59.6) * mm, "end": v(26.32, 81.51) * mm});
            skLineSegment(sketch, "E174.0", {"start": v(26.32, 81.51) * mm, "end": v(7.32, 81.51) * mm});
            skLineSegment(sketch, "E175.0", {"start": v(7.32, 81.51) * mm, "end": v(7.32, 57.51) * mm});
            skLineSegment(sketch, "E176.0", {"start": v(7.32, 57.51) * mm, "end": v(8.32, 57.51) * mm});
            skLineSegment(sketch, "E177.0", {"start": v(56.32, 81.51) * mm, "end": v(37.32, 81.51) * mm});
            skLineSegment(sketch, "E178.0", {"start": v(37.32, 81.51) * mm, "end": v(37.32, 57.51) * mm});
            skLineSegment(sketch, "E179.0", {"start": v(56.32, 59.6) * mm, "end": v(56.32, 81.51) * mm});
            skLineSegment(sketch, "E180.0", {"start": v(56.32, 59.6) * mm, "end": v(57.02, 58.92) * mm});
            skLineSegment(sketch, "E181.0", {"start": v(57.02, 58.92) * mm, "end": v(56.32, 58.2) * mm});
            skLineSegment(sketch, "E182.0", {"start": v(56.32, 57.51) * mm, "end": v(56.32, 58.2) * mm});
            skLineSegment(sketch, "E183.0", {"start": v(55.64, 57.51) * mm, "end": v(56.32, 57.51) * mm});
            skLineSegment(sketch, "E184.0", {"start": v(55.64, 57.51) * mm, "end": v(55.32, 57.19) * mm});
            skLineSegment(sketch, "E185.0", {"start": v(55.32, 55.69) * mm, "end": v(55.32, 57.19) * mm});
            skLineSegment(sketch, "E186.0", {"start": v(55.32, 55.69) * mm, "end": v(65.5, 45.72) * mm});
            skLineSegment(sketch, "E187.0", {"start": v(65.5, 45.72) * mm, "end": v(55, 35) * mm});
            skLineSegment(sketch, "E188.0", {"start": v(55, 35) * mm, "end": v(44.07, 45.7) * mm});
            skLineSegment(sketch, "E189.0", {"start": v(44.07, 45.7) * mm, "end": v(41.62, 43.2) * mm});
            skLineSegment(sketch, "E190.0", {"start": v(41.62, 43.2) * mm, "end": v(36.62, 48.1) * mm});
            skLineSegment(sketch, "E191.0", {"start": v(36.62, 48.1) * mm, "end": v(38.32, 49.84) * mm});
            skLineSegment(sketch, "E192.0", {"start": v(38.32, 57.51) * mm, "end": v(38.32, 49.84) * mm});
            skLineSegment(sketch, "E193.0", {"start": v(37.32, 57.51) * mm, "end": v(38.32, 57.51) * mm});
            skLineSegment(sketch, "E194.0", {"start": v(95.5, 45.72) * mm, "end": v(85, 35) * mm});
            skLineSegment(sketch, "E195.0", {"start": v(85.32, 55.69) * mm, "end": v(95.5, 45.72) * mm});
            skLineSegment(sketch, "E196.0", {"start": v(85, 35) * mm, "end": v(74.07, 45.7) * mm});
            skLineSegment(sketch, "E197.0", {"start": v(74.07, 45.7) * mm, "end": v(71.62, 43.2) * mm});
            skLineSegment(sketch, "E198.0", {"start": v(71.62, 43.2) * mm, "end": v(66.62, 48.1) * mm});
            skLineSegment(sketch, "E199.0", {"start": v(66.62, 48.1) * mm, "end": v(68.32, 49.84) * mm});
            skLineSegment(sketch, "E200.0", {"start": v(68.32, 57.51) * mm, "end": v(68.32, 49.84) * mm});
            skLineSegment(sketch, "E201.0", {"start": v(67.32, 57.51) * mm, "end": v(68.32, 57.51) * mm});
            skLineSegment(sketch, "E202.0", {"start": v(67.32, 81.51) * mm, "end": v(67.32, 57.51) * mm});
            skLineSegment(sketch, "E203.0", {"start": v(86.32, 81.51) * mm, "end": v(67.32, 81.51) * mm});
            skLineSegment(sketch, "E204.0", {"start": v(86.32, 59.6) * mm, "end": v(86.32, 81.51) * mm});
            skLineSegment(sketch, "E205.0", {"start": v(86.32, 59.6) * mm, "end": v(87.02, 58.92) * mm});
            skLineSegment(sketch, "E206.0", {"start": v(87.02, 58.92) * mm, "end": v(86.32, 58.2) * mm});
            skLineSegment(sketch, "E207.0", {"start": v(86.32, 57.51) * mm, "end": v(86.32, 58.2) * mm});
            skLineSegment(sketch, "E208.0", {"start": v(85.64, 57.51) * mm, "end": v(86.32, 57.51) * mm});
            skLineSegment(sketch, "E209.0", {"start": v(85.64, 57.51) * mm, "end": v(85.32, 57.19) * mm});
            skLineSegment(sketch, "E210.0", {"start": v(85.32, 55.69) * mm, "end": v(85.32, 57.19) * mm});
            skLineSegment(sketch, "E211.0", {"start": v(103, 53) * mm, "end": v(107.25, 53) * mm});
            skLineSegment(sketch, "E212.0", {"start": v(107.25, 54.5) * mm, "end": v(107.25, 53) * mm});
            skArc(sketch, "E213.0", {"start": v(107.25, 54.5) * mm, "mid": v(106.52, 56.27) * mm, "end": v(104.75, 57) * mm});
            skLineSegment(sketch, "E214.0", {"start": v(97.25, 57) * mm, "end": v(104.75, 57) * mm});
            skArc(sketch, "E215.0", {"start": v(97.25, 57) * mm, "mid": v(95.48, 56.27) * mm, "end": v(94.75, 54.5) * mm});
            skLineSegment(sketch, "E216.0", {"start": v(94.75, 53) * mm, "end": v(94.75, 54.5) * mm});
            skLineSegment(sketch, "E217.0", {"start": v(94.75, 53) * mm, "end": v(99, 53) * mm});
            skLineSegment(sketch, "E218.0", {"start": v(99, 40) * mm, "end": v(99, 53) * mm});
            skLineSegment(sketch, "E219.0", {"start": v(99, 40) * mm, "end": v(100, 37) * mm});
            skLineSegment(sketch, "E220.0", {"start": v(100, 37) * mm, "end": v(102, 37) * mm});
            skLineSegment(sketch, "E221.0", {"start": v(102, 37) * mm, "end": v(103, 40) * mm});
            skLineSegment(sketch, "E222.0", {"start": v(103, 53) * mm, "end": v(103, 40) * mm});
            skLineSegment(sketch, "E223.0", {"start": v(120.5, 53) * mm, "end": v(120.5, 40) * mm});
            skLineSegment(sketch, "E224.0", {"start": v(120.5, 53) * mm, "end": v(124.75, 53) * mm});
            skLineSegment(sketch, "E225.0", {"start": v(124.75, 54.5) * mm, "end": v(124.75, 53) * mm});
            skArc(sketch, "E226.0", {"start": v(124.75, 54.5) * mm, "mid": v(124.02, 56.27) * mm, "end": v(122.25, 57) * mm});
            skLineSegment(sketch, "E227", {"start": v(122.25, 57) * mm, "end": v(114.75, 57) * mm});
            skArc(sketch, "E228.0", {"start": v(114.75, 57) * mm, "mid": v(112.98, 56.27) * mm, "end": v(112.25, 54.5) * mm});
            skLineSegment(sketch, "E229.0", {"start": v(112.25, 53) * mm, "end": v(112.25, 54.5) * mm});
            skLineSegment(sketch, "E230.0", {"start": v(112.25, 53) * mm, "end": v(116.5, 53) * mm});
            skLineSegment(sketch, "E231.0", {"start": v(116.5, 40) * mm, "end": v(116.5, 53) * mm});
            skLineSegment(sketch, "E232.0", {"start": v(116.5, 40) * mm, "end": v(117.5, 37) * mm});
            skLineSegment(sketch, "E233.0", {"start": v(117.5, 37) * mm, "end": v(119.5, 37) * mm});
            skLineSegment(sketch, "E234.0", {"start": v(119.5, 37) * mm, "end": v(120.5, 40) * mm});
            skLineSegment(sketch, "E235.0", {"start": v(117.5, 62) * mm, "end": v(119.5, 62) * mm});
            skLineSegment(sketch, "E236.0", {"start": v(119.5, 62) * mm, "end": v(121.5, 65) * mm});
            skLineSegment(sketch, "E237.0", {"start": v(121.5, 78) * mm, "end": v(121.5, 65) * mm});
            skLineSegment(sketch, "E238.0", {"start": v(115.5, 65) * mm, "end": v(115.5, 78) * mm});
            skLineSegment(sketch, "E239.0", {"start": v(115.5, 65) * mm, "end": v(117.5, 62) * mm});
            skLineSegment(sketch, "E240.0", {"start": v(112.25, 78) * mm, "end": v(115.5, 78) * mm});
            skLineSegment(sketch, "E241.0", {"start": v(112.25, 78) * mm, "end": v(112.25, 79.5) * mm});
            skArc(sketch, "E242.0", {"start": v(114.75, 82) * mm, "mid": v(112.98, 81.27) * mm, "end": v(112.25, 79.5) * mm});
            skLineSegment(sketch, "E243.0", {"start": v(114.75, 82) * mm, "end": v(122.25, 82) * mm});
            skArc(sketch, "E244.0", {"start": v(124.75, 79.5) * mm, "mid": v(124.02, 81.27) * mm, "end": v(122.25, 82) * mm});
            skLineSegment(sketch, "E245.0", {"start": v(124.75, 79.5) * mm, "end": v(124.75, 78) * mm});
            skLineSegment(sketch, "E246.0", {"start": v(121.5, 78) * mm, "end": v(124.75, 78) * mm});
            skLineSegment(sketch, "E247.0", {"start": v(104, 78) * mm, "end": v(107.25, 78) * mm});
            skLineSegment(sketch, "E248.0", {"start": v(107.25, 79.5) * mm, "end": v(107.25, 78) * mm});
            skArc(sketch, "E249.0", {"start": v(107.25, 79.5) * mm, "mid": v(106.52, 81.27) * mm, "end": v(104.75, 82) * mm});
            skLineSegment(sketch, "E250.0", {"start": v(97.25, 82) * mm, "end": v(104.75, 82) * mm});
            skArc(sketch, "E251.0", {"start": v(97.25, 82) * mm, "mid": v(95.48, 81.27) * mm, "end": v(94.75, 79.5) * mm});
            skLineSegment(sketch, "E252.0", {"start": v(94.75, 78) * mm, "end": v(94.75, 79.5) * mm});
            skLineSegment(sketch, "E253.0", {"start": v(94.75, 78) * mm, "end": v(98, 78) * mm});
            skLineSegment(sketch, "E254.0", {"start": v(98, 65) * mm, "end": v(98, 78) * mm});
            skLineSegment(sketch, "E255.0", {"start": v(98, 65) * mm, "end": v(100, 62) * mm});
            skLineSegment(sketch, "E256.0", {"start": v(100, 62) * mm, "end": v(102, 62) * mm});
            skLineSegment(sketch, "E257.0", {"start": v(102, 62) * mm, "end": v(104, 65) * mm});
            skLineSegment(sketch, "E258.0", {"start": v(104, 78) * mm, "end": v(104, 65) * mm});
            skLineSegment(sketch, "E259.0", {"start": v(57.75, 26) * mm, "end": v(58.75, 26) * mm});
            skSolve(sketch);
        }
        {
            var Q0;
            Q0 = qSketchRegion(id + "F21", true);
            extrude(context, id + "F22", {"entities" : qUnion([Q0]), "operationType" : NewBodyOperationType.ADD, "oppositeDirection" : true, "depth" : 5 * mm, "offsetDistance" : 25 * mm});
        }
    });
